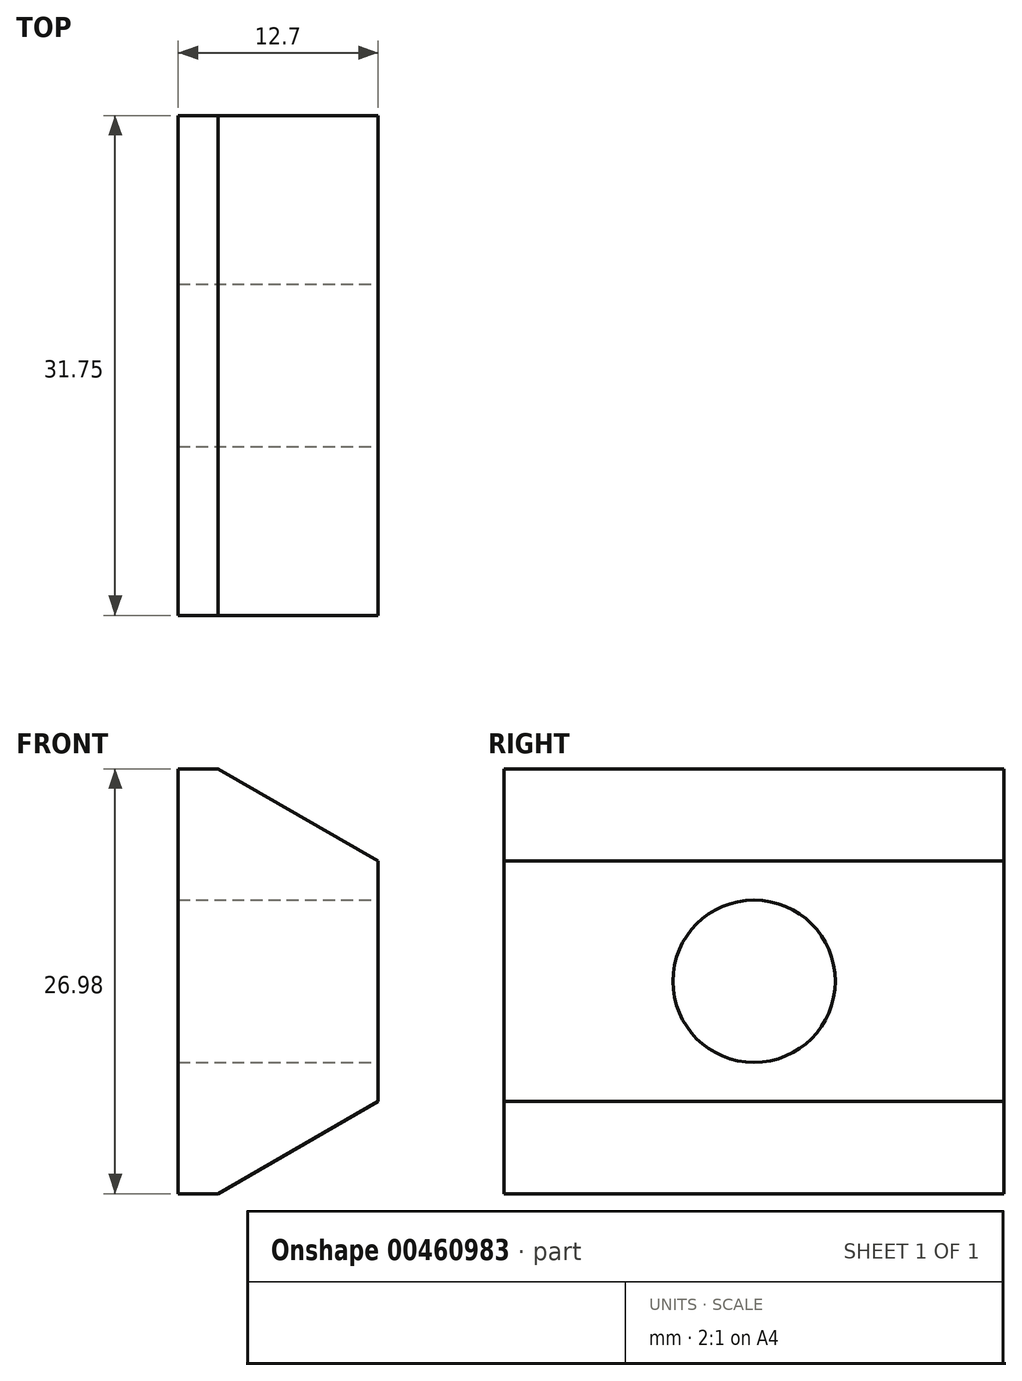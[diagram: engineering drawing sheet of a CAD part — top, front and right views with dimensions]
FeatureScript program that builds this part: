
annotation { "Feature Type Name" : "Feature", "Feature Type Description" : "" }
export const myFeature = defineFeature(function(context is Context, id is Id, definition is map)
    precondition{}
    {
        {
            var Q0;
            Q0=qCreatedBy(makeId("Front.planeOp"),FACE);
            var sketch = newSketch(context, id + "F0", { "sketchPlane" : qUnion([Q0])});
            skLineSegment(sketch, "E0.bottom", {"start": v(-58.77, 56.12) * mm, "end": v(-56.23, 56.12) * mm});
            skLineSegment(sketch, "E0.top", {"start": v(-58.77, 29.14) * mm, "end": v(-56.23, 29.14) * mm});
            skLineSegment(sketch, "E0.left", {"start": v(-58.77, 56.12) * mm, "end": v(-58.77, 29.14) * mm});
            skLineSegment(sketch, "E0.right", {"start": v(-46.07, 50.26) * mm, "end": v(-46.07, 35) * mm});
            skLineSegment(sketch, "E1", {"start": v(-56.23, 56.12) * mm, "end": v(-46.07, 50.26) * mm});
            skLineSegment(sketch, "E2", {"start": v(-56.23, 29.14) * mm, "end": v(-46.07, 35) * mm});
            skSolve(sketch);
        }
        {
            var Q0;
            Q0=makeQuery(id+"F0.imprint","IMPRINT",FACE,{"disambiguationData":[TD([[makeQuery(id+"F0.imprint","IMPRINT",EDGE,{"derivedFrom":sQuery(id+"F0.wireOp",EDGE,"E0.bottom")}),-1.0]])]});
            extrude(context, id + "F1", {"entities" : qUnion([Q0]), "depth" : 31.75 * mm});
        }
        {
            var Q0;
            Q0=makeQuery(id+"F1.opExtrude","SWEPT_FACE",FACE,{"disambiguationData":[OSD([sQuery(id+"F0.wireOp",EDGE,"E0.right")])]});
            var sketch = newSketch(context, id + "F2", { "sketchPlane" : qUnion([Q0])});
            skLineSegment(sketch, "E3", {"start": v(-15.88, 50.26) * mm, "end": v(-15.88, 35) * mm});
            skPoint(sketch, "E4", {"position": v(-15.88, 42.63) * mm});
            skSolve(sketch);
        }
        {
            var Q0;
            Q0=sQuery(id+"F2.wireOp",VERTEX,"E4");
            var Q1;
            Q1=makeQuery(id+"F1.opExtrude","SWEPT_BODY",BODY,{"disambiguationData":[OSD([sQuery(id+"F0.wireOp",EDGE,"E0.bottom"),sQuery(id+"F0.wireOp",EDGE,"E0.top"),sQuery(id+"F0.wireOp",EDGE,"E0.left"),sQuery(id+"F0.wireOp",EDGE,"E0.right"),sQuery(id+"F0.wireOp",EDGE,"E1"),sQuery(id+"F0.wireOp",EDGE,"E2")])]});
            hole(context, id + "F3", {"style" : HoleStyle.SIMPLE, "endStyle" : HoleEndStyle.THROUGH, "holeDiameter" : 10.3 * mm, "isTappedThrough" : true, "tappedDepth" : 12.7 * mm, "tapClearance" : 3, "startFromSketch" : true, "locations" : qUnion([Q0]), "scope" : qUnion([Q1])});
        }
    });
